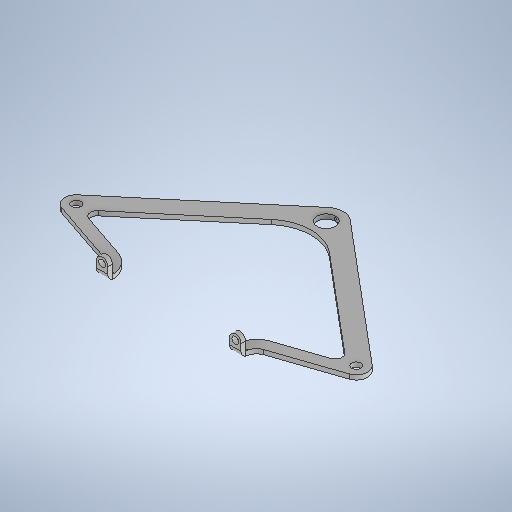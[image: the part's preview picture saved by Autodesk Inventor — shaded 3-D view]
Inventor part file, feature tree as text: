
AUTODESK INVENTOR PART (.ipt)
format: ipt  version: 2025.1 (Build 291241000, 241)  size: 379,392 bytes
history: native  units: mm
features: sketch x6, hole x4, extrude x2, plane x2, fillet x2, projected_geometry x2
ambient origin geometry x8: Origin, YZ Plane, XZ Plane, XY Plane, X Axis, Y Axis, Z Axis, Center Point
bodies: Solid1 (feature_tree)
feature tree (18):
  extrude  "Extrusion1"  Depth=22.0mm
  plane  "Work Plane5"
  extrude  "Extrusion2"  Depth=3.0mm
  fillet  "Fillet3"  Radius=3.0mm
  fillet  "Fillet4"  Radius=5.0mm
  hole  "Hole2"  [1 undecoded]
  hole  "Hole3"  [1 undecoded]
  hole  "Hole4"  [1 undecoded]
  plane  "Work Plane6"
  hole  "Hole5"  [1 undecoded]
  sketch  "Sketch1"  dims[d0=40.0mm d1=22.0mm]
  sketch  "Sketch5"  dims[d2=8.0mm d3=3.0mm d4=3.0mm d5=5.0mm]
  projected_geometry  "Projected Loop1"
  projected_geometry  "Projected Loop2"
  sketch  "Sketch7"  dims[d6=5.0mm d7=5.0mm]
  sketch  "Sketch8"  dims[d8=5.0mm d9=7.5mm]
  sketch  "Sketch9"  dims[d10=8.0mm d11=124.0mm]
  sketch  "Sketch10"  dims[d12=62.0mm d13=10.0mm d14=5.0mm d15=10.0mm d16=5.0mm d17=5.0mm d18=48.760903mm d20=29.5mm d21=59.0mm d22=2.0mm d23=0.0mm d28=0.0mm d29=2.5mm d30=2.5mm d31=4.0mm d32=4.0mm d33=2.0mm d34=0.0mm d44=1.0mm d45=3.0mm d46=3.0mm d47=6.0mm d48=4.0mm d49=2.0mm d50=90.0deg d51=8.0mm d52=0.0mm d53=4.0mm d54=6.0mm d55=4.0mm d56=2.0mm d57=90.0deg d58=8.0mm d59=0.0mm d60=8.0mm d61=6.0mm d62=4.0mm d63=2.0mm d64=90.0deg d65=8.0mm d66=0.0mm d67=56.5mm d68=1.0mm d69=6.0mm d70=4.0mm d71=2.0mm d72=90.0deg d73=4.0mm d74=0.0mm]
note: 4 required parameter values undecoded (feature->parameter linkage not recoverable at this tier; creation-order binding heuristic only, values carry confidence <= 0.55)
